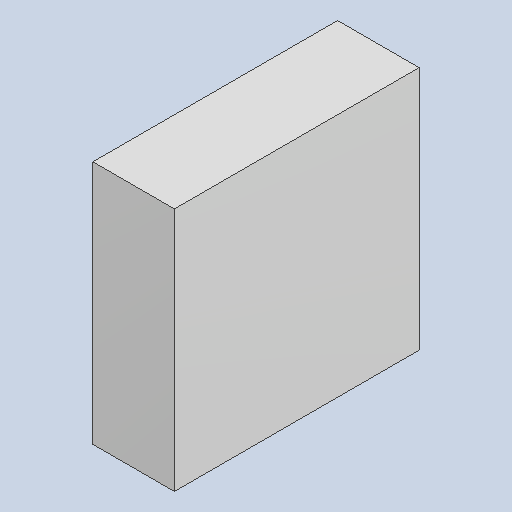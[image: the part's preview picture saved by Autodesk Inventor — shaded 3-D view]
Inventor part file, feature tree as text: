
AUTODESK INVENTOR PART (.ipt)
format: ipt  version: 2023.4 (Build 274418000, 418)  size: 81,408 bytes
history: native  units: mm
features: extrude x1
ambient origin geometry x8: Origin, YZ Plane, XZ Plane, XY Plane, X Axis, Y Axis, Z Axis, Center Point
bodies: Solid1 (feature_tree)
feature tree (1):
  extrude  "Extruded_40"  [1 undecoded]
note: 1 required parameter value undecoded (feature->parameter linkage not recoverable at this tier; creation-order binding heuristic only, values carry confidence <= 0.55)
